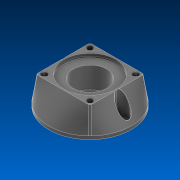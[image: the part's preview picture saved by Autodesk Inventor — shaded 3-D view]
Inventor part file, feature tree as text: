
AUTODESK INVENTOR PART (.ipt)
format: ipt  version: 2022.2 (Build 262287000, 287)  size: 683,008 bytes
history: native  units: in
note: dims shown in document units (in); Inventor stores cm internally (conversion verified against a paired STEP export)
features: fillet x1
ambient origin geometry x8: Origin, YZ Plane, XZ Plane, XY Plane, X Axis, Y Axis, Z Axis, Center Point
bodies: Solid1 (feature_tree)
feature tree (1):
  fillet  "Fillet3"  [1 undecoded]
note: 1 required parameter value undecoded (feature->parameter linkage not recoverable at this tier; creation-order binding heuristic only, values carry confidence <= 0.55)
